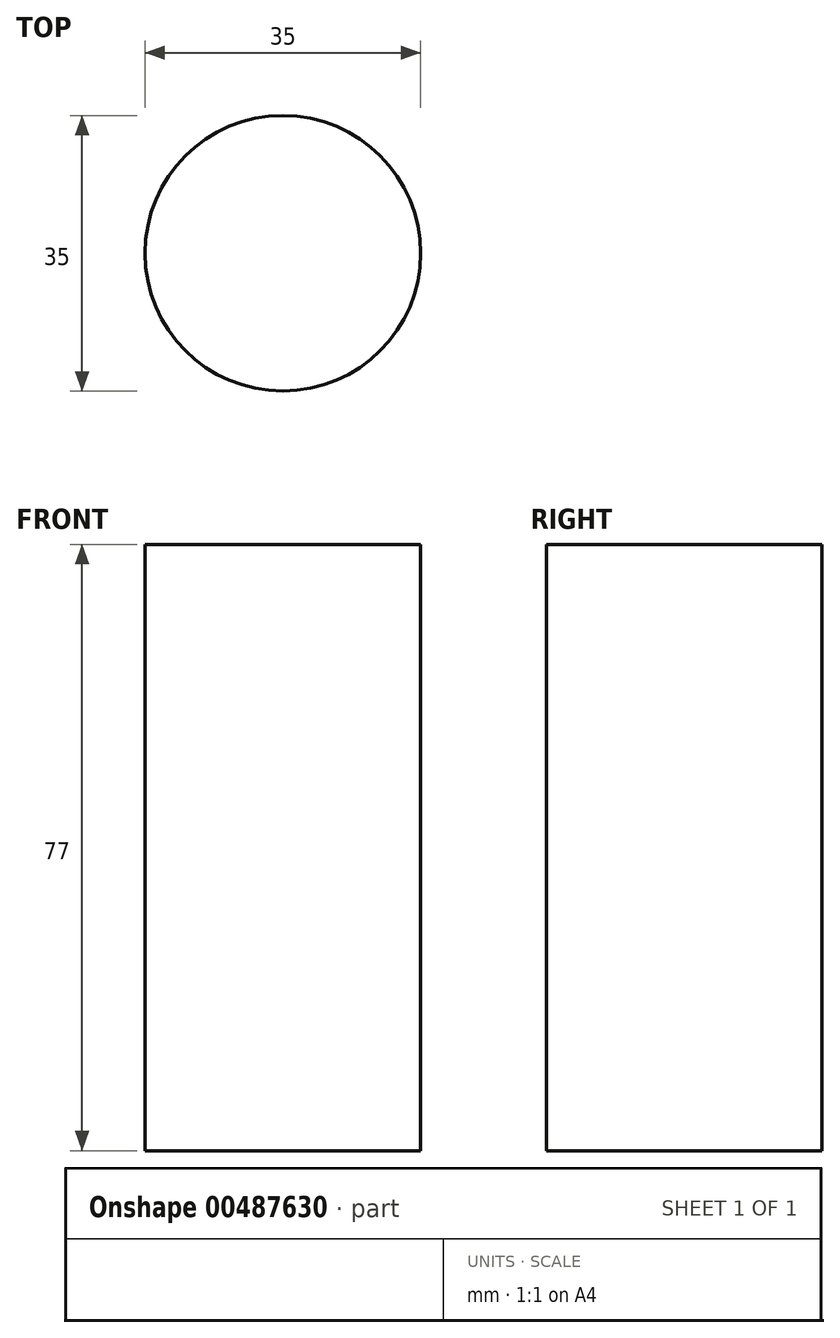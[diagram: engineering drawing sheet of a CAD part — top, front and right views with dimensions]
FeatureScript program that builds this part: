
annotation { "Feature Type Name" : "Feature", "Feature Type Description" : "" }
export const myFeature = defineFeature(function(context is Context, id is Id, definition is map)
    precondition{}
    {
        {
            var Q0;
            Q0=qCreatedBy(makeId("Top.planeOp"),FACE);
            var sketch = newSketch(context, id + "F0", { "sketchPlane" : qUnion([Q0])});
            skCircle(sketch, "E0", {"center": v(0, 0) * mm, "radius": 17.5 * mm});
            skSolve(sketch);
        }
        {
            var Q0;
            Q0 = qSketchRegion(id + "F0", true);
            extrude(context, id + "F1", {"entities" : qUnion([Q0]), "depth" : 77 * mm});
        }
        {
            var Q0;
            Q0=qCreatedBy(makeId("Right.planeOp"),FACE);
            cPlane(context, id + "F2", {"entities" : qUnion([Q0]), "cplaneType" : CPlaneType.OFFSET, "offset" : 25 * mm, "width" : 150 * mm, "height" : 150 * mm});
        }
        {
            var Q0;
            Q0=qCreatedBy(id+"F2.planeOp",FACE);
            var sketch = newSketch(context, id + "F3", { "sketchPlane" : qUnion([Q0])});
            skLineSegment(sketch, "E1", {"start": v(0, 0) * mm, "end": v(0, 77) * mm, "construction": true});
            skLineSegment(sketch, "E2.0", {"start": v(-17.5, 77) * mm, "end": v(17.5, 77) * mm});
            skPoint(sketch, "E3", {"position": v(0, 38.5) * mm});
            skSolve(sketch);
        }
    });
